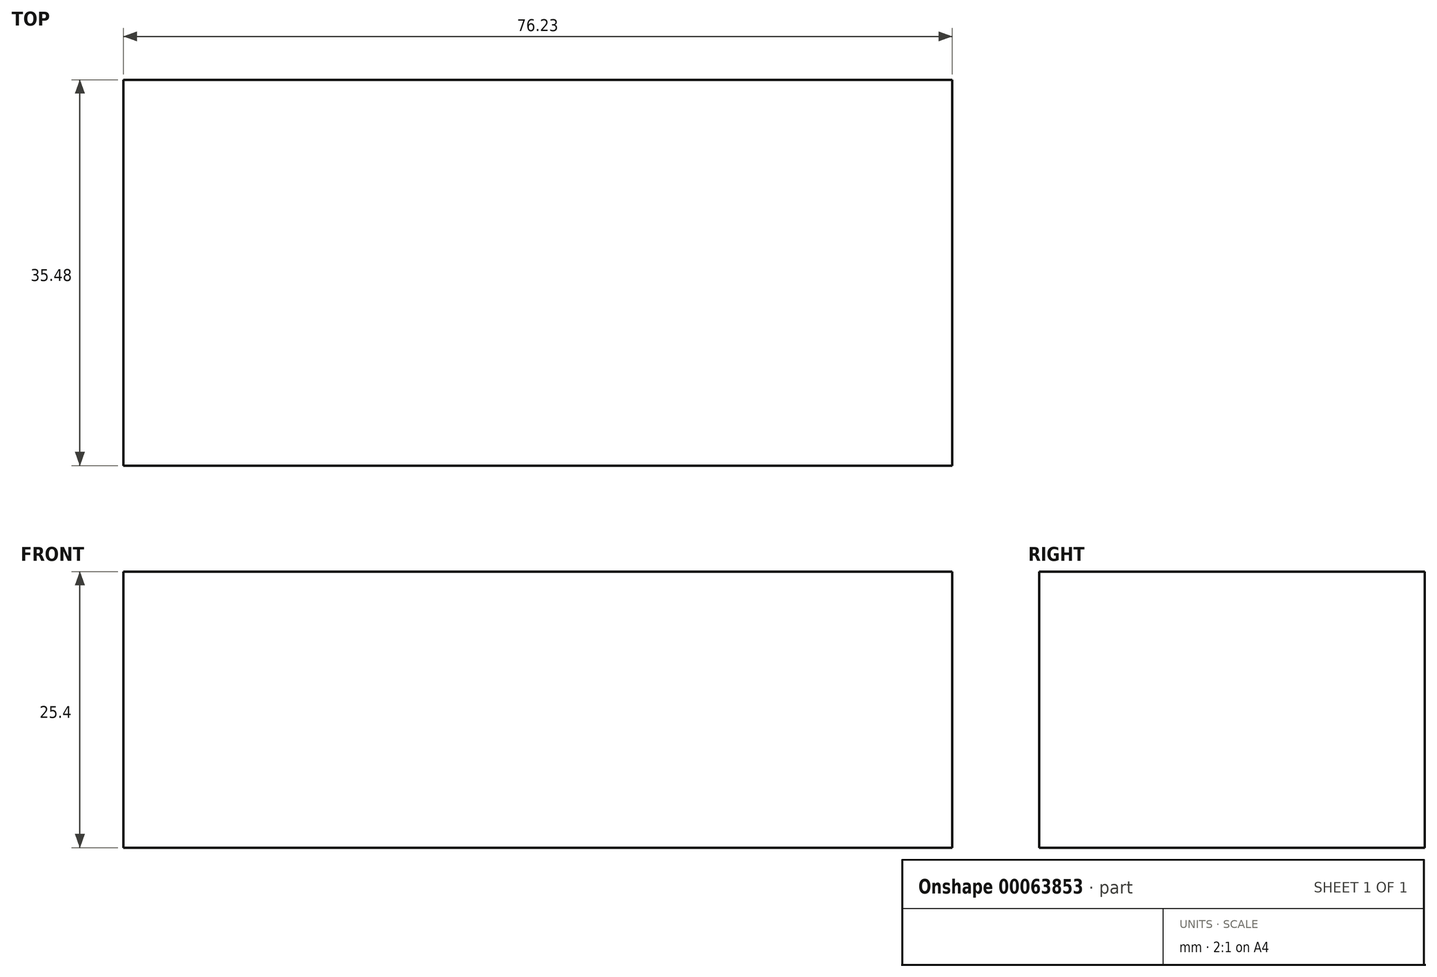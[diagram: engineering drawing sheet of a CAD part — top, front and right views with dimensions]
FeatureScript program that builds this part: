
annotation { "Feature Type Name" : "Feature", "Feature Type Description" : "" }
export const myFeature = defineFeature(function(context is Context, id is Id, definition is map)
    precondition{}
    {
        {
            var Q0;
            Q0=qCreatedBy(makeId("Top.planeOp"),FACE);
            var sketch = newSketch(context, id + "F0", { "sketchPlane" : qUnion([Q0])});
            skLineSegment(sketch, "E0.bottom", {"start": v(0, 0) * mm, "end": v(-76.23, 0) * mm});
            skLineSegment(sketch, "E0.top", {"start": v(0, 35.17) * mm, "end": v(-76.23, 35.17) * mm});
            skLineSegment(sketch, "E0.left", {"start": v(0, 0) * mm, "end": v(0, 35.17) * mm});
            skLineSegment(sketch, "E0.right", {"start": v(-76.23, 0) * mm, "end": v(-76.23, 35.17) * mm});
            skSolve(sketch);
        }
        {
            var Q0;
            Q0=makeQuery(id+"F0.imprint","IMPRINT",FACE,{"disambiguationData":[TD([[makeQuery(id+"F0.imprint","IMPRINT",EDGE,{"derivedFrom":sQuery(id+"F0.wireOp",EDGE,"E0.bottom")}),-1.0]])]});
            extrude(context, id + "F1", {"entities" : qUnion([Q0]), "depth" : 25.4 * mm});
        }
        {
            var Q0;
            Q0=makeQuery(id+"F1.opExtrude","SWEPT_FACE",FACE,{"disambiguationData":[OSD([sQuery(id+"F0.wireOp",EDGE,"E0.top")])]});
            extrude(context, id + "F2", {"entities" : qUnion([Q0]), "operationType" : NewBodyOperationType.ADD, "depth" : 0.3 * mm});
        }
    });
